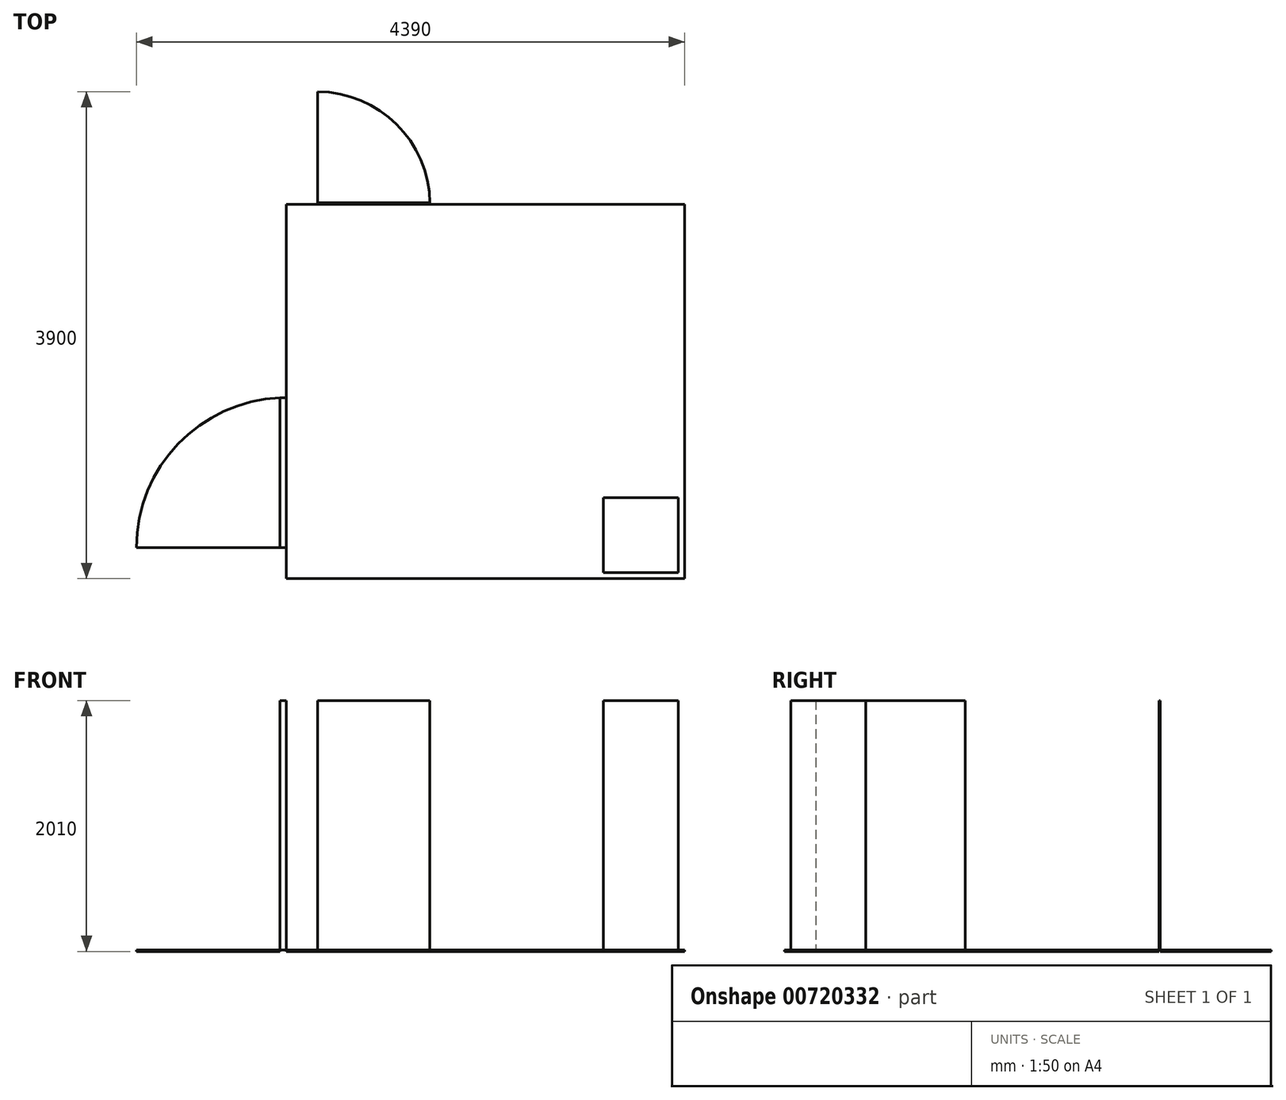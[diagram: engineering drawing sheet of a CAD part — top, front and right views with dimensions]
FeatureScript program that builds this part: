
annotation { "Feature Type Name" : "Feature", "Feature Type Description" : "" }
export const myFeature = defineFeature(function(context is Context, id is Id, definition is map)
    precondition{}
    {
        {
            var Q0;
            Q0=qCreatedBy(makeId("Top.planeOp"),FACE);
            var sketch = newSketch(context, id + "F0", { "sketchPlane" : qUnion([Q0])});
            skLineSegment(sketch, "E0.bottom", {"start": v(1595, -1500) * mm, "end": v(-1595, -1500) * mm});
            skLineSegment(sketch, "E0.top", {"start": v(1595, 1500) * mm, "end": v(-1595, 1500) * mm});
            skLineSegment(sketch, "E0.left", {"start": v(1595, -1500) * mm, "end": v(1595, 1500) * mm});
            skLineSegment(sketch, "E0.right", {"start": v(-1595, -1500) * mm, "end": v(-1595, 1500) * mm});
            skPoint(sketch, "E0.middle", {"position": v(0, 0) * mm});
            skSolve(sketch);
        }
        {
            var Q0;
            Q0 = qSketchRegion(id + "F0", true);
            extrude(context, id + "F1", {"entities" : qUnion([Q0]), "depth" : 10 * mm, "offsetDistance" : 25 * mm});
        }
        {
            var Q0;
            Q0=makeQuery(id+"F1.opExtrude","CAP_FACE",FACE,{"disambiguationData":[OSD([sQuery(id+"F0.wireOp",EDGE,"E0.bottom"),sQuery(id+"F0.wireOp",EDGE,"E0.top"),sQuery(id+"F0.wireOp",EDGE,"E0.left"),sQuery(id+"F0.wireOp",EDGE,"E0.right")])],"isStart":false});
            var sketch = newSketch(context, id + "F2", { "sketchPlane" : qUnion([Q0])});
            skLineSegment(sketch, "E1.bottom", {"start": v(-1345, 1500) * mm, "end": v(-445, 1500) * mm});
            skLineSegment(sketch, "E1.top", {"start": v(-1345, 1510) * mm, "end": v(-445, 1510) * mm});
            skLineSegment(sketch, "E1.left", {"start": v(-1345, 1500) * mm, "end": v(-1345, 1510) * mm});
            skLineSegment(sketch, "E1.right", {"start": v(-445, 1500) * mm, "end": v(-445, 1510) * mm});
            skLineSegment(sketch, "E2.bottom", {"start": v(-1595, -1250) * mm, "end": v(-1645, -1250) * mm});
            skLineSegment(sketch, "E2.top", {"start": v(-1595, -50) * mm, "end": v(-1645, -50) * mm});
            skLineSegment(sketch, "E2.left", {"start": v(-1595, -1250) * mm, "end": v(-1595, -50) * mm});
            skLineSegment(sketch, "E2.right", {"start": v(-1645, -1250) * mm, "end": v(-1645, -50) * mm});
            skSolve(sketch);
        }
        {
            var Q0;
            Q0 = qSketchRegion(id + "F2", true);
            extrude(context, id + "F3", {"entities" : qUnion([Q0]), "depth" : 2000 * mm, "offsetDistance" : 25 * mm});
        }
        {
            var Q0;
            Q0=makeQuery(id+"F1.opExtrude","CAP_FACE",FACE,{"disambiguationData":[OSD([sQuery(id+"F0.wireOp",EDGE,"E0.bottom"),sQuery(id+"F0.wireOp",EDGE,"E0.top"),sQuery(id+"F0.wireOp",EDGE,"E0.left"),sQuery(id+"F0.wireOp",EDGE,"E0.right")])],"isStart":false});
            var sketch = newSketch(context, id + "F4", { "sketchPlane" : qUnion([Q0])});
            skLineSegment(sketch, "E3.bottom", {"start": v(1545, -1450) * mm, "end": v(945, -1450) * mm});
            skLineSegment(sketch, "E3.top", {"start": v(1545, -850) * mm, "end": v(945, -850) * mm});
            skLineSegment(sketch, "E3.left", {"start": v(1545, -1450) * mm, "end": v(1545, -850) * mm});
            skLineSegment(sketch, "E3.right", {"start": v(945, -1450) * mm, "end": v(945, -850) * mm});
            skPoint(sketch, "E3.middle", {"position": v(1245, -1150) * mm});
            skSolve(sketch);
        }
        {
            var Q0;
            Q0 = qSketchRegion(id + "F4", true);
            extrude(context, id + "F5", {"entities" : qUnion([Q0]), "depth" : 2000 * mm, "offsetDistance" : 25 * mm});
        }
        {
            var Q0;
            Q0=makeQuery(id+"F3.opExtrude","CAP_FACE",FACE,{"disambiguationData":[OSD([sQuery(id+"F2.wireOp",EDGE,"E2.bottom"),sQuery(id+"F2.wireOp",EDGE,"E2.top"),sQuery(id+"F2.wireOp",EDGE,"E2.left"),sQuery(id+"F2.wireOp",EDGE,"E2.right")])],"isStart":true});
            var sketch = newSketch(context, id + "F6", { "sketchPlane" : qUnion([Q0])});
            skArc(sketch, "E4", {"start": v(-2795, 1250) * mm, "mid": v(-2443.53, 401.47) * mm, "end": v(-1595, 50) * mm});
            skLineSegment(sketch, "E5", {"start": v(-1595, 1250) * mm, "end": v(-2795, 1250) * mm});
            skSolve(sketch);
        }
        {
            var Q0;
            Q0=makeQuery(id+"F3.opExtrude","CAP_FACE",FACE,{"disambiguationData":[OSD([sQuery(id+"F2.wireOp",EDGE,"E1.bottom"),sQuery(id+"F2.wireOp",EDGE,"E1.top"),sQuery(id+"F2.wireOp",EDGE,"E1.left"),sQuery(id+"F2.wireOp",EDGE,"E1.right")])],"isStart":true});
            var sketch = newSketch(context, id + "F7", { "sketchPlane" : qUnion([Q0])});
            skArc(sketch, "E6", {"start": v(-1345, -2400) * mm, "mid": v(-708.6, -2136.4) * mm, "end": v(-445, -1500) * mm});
            skLineSegment(sketch, "E7", {"start": v(-1345, -1500) * mm, "end": v(-1345, -2400) * mm});
            skSolve(sketch);
        }
        {
            var Q0;
            {var subQ0=sQuery(id+"F7.wireOp",EDGE,"E7");var subQ1=sQuery(id+"F7.wireOp",EDGE,"E6");var subQ2=makeQuery(id+"F7.imprint","INTERSECT",VERTEX,{"derivedFrom":[subQ1,subQ0]});Q0=makeQuery(id+"F7.imprint","IMPRINT",FACE,{"disambiguationData":[TD([[makeQuery(id+"F7.imprint","IMPRINT",EDGE,{"disambiguationData":[TD([[subQ2,-1.0]])],"derivedFrom":subQ1}),1.0]])]});}
            extrude(context, id + "F8", {"entities" : qUnion([Q0]), "operationType" : NewBodyOperationType.ADD, "depth" : 10 * mm, "offsetDistance" : 25 * mm});
        }
        {
            var Q0;
            {var subQ0=sQuery(id+"F6.wireOp",EDGE,"E5");var subQ1=sQuery(id+"F6.wireOp",EDGE,"E4");var subQ2=makeQuery(id+"F6.imprint","INTERSECT",VERTEX,{"derivedFrom":[subQ1,subQ0]});Q0=makeQuery(id+"F6.imprint","IMPRINT",FACE,{"disambiguationData":[TD([[makeQuery(id+"F6.imprint","IMPRINT",EDGE,{"disambiguationData":[TD([[subQ2,-1.0]])],"derivedFrom":subQ1}),1.0]])]});}
            extrude(context, id + "F9", {"entities" : qUnion([Q0]), "operationType" : NewBodyOperationType.ADD, "depth" : 10 * mm, "offsetDistance" : 25 * mm});
        }
    });
